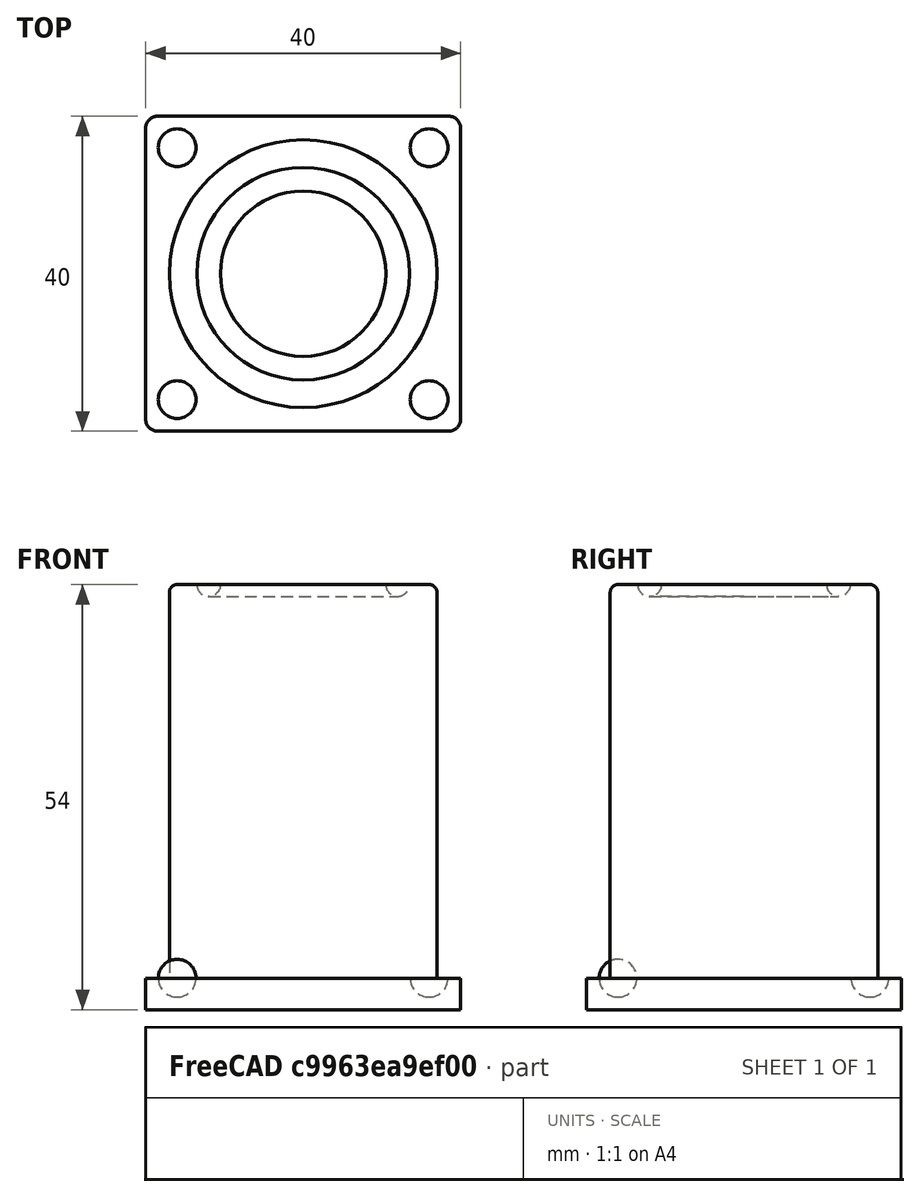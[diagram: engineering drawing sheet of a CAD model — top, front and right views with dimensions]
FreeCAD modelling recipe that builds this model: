
FCSTD DOCUMENT  (FreeCAD 0.21R33694 (Git))
Label: OJT1_T15R03
License: All rights reserved
LicenseURL: http://en.wikipedia.org/wiki/All_rights_reserved
objects: Part::Fillet×2, Part::Cut×2, Part::Box×1, Part::Cylinder×1, Part::Torus×1, Part::Sphere×1, Part::FeaturePython×1, Part::Fuse×1
note: 9 computed .brp shape members not serialized (recipe doc carries the construction recipe); baked Part::Feature solids carry a one-line shape summary decoded from their .brp

FEATURE [Part::Box] Box  label="Cube"
  AttacherType = Attacher::AttachEngine3D
  Height = 4
  Length = 40
  Width = 40
FEATURE [Part::Cylinder] Cylinder
  Angle = 360
  AttacherType = Attacher::AttachEngine3D
  FirstAngle = 0
  Height = 50
  Radius = 17
  SecondAngle = 0
FEATURE [Part::Torus] Torus  label="part_cilindre"
  Angle1 = -180
  Angle2 = 180
  Angle3 = 360
  AttacherType = Attacher::AttachEngine3D
  Placement = pos=(0,0,50) rot=(0,0,1;0rad)
  Radius1 = 12
  Radius2 = 1.5
FEATURE [Part::Fillet] Fillet  label="cilindre_sense_acabar"
  Base = -> Box
  Edges = 4 edges r=1.5: [Edge1,Edge3,Edge5,Edge7]
FEATURE [Part::Fillet] Fillet001  label="cilindre"
  Base = -> Cylinder
  Edges = 1 edges r=1: [Edge3]
FEATURE [Part::Sphere] Sphere
  Angle1 = -90
  Angle2 = 90
  Angle3 = 360
  AttacherType = Attacher::AttachEngine3D
  Placement = pos=(4,4,4) rot=(0,0,1;0rad)
  Radius = 2.4
FEATURE [Part::FeaturePython] Array  # Draft array (typed FeaturePython)
  AlwaysSyncPlacement = false
  Angle = 360
  ArrayType = 0
  Axis = (0,0,1)
  Base = -> Sphere
  Center = (0,0,0)
  Count = 4
  ExpandArray = false
  Fuse = false
  IntervalAxis = (0,0,0)
  IntervalX = (32,0,0)
  IntervalY = (0,32,0)
  IntervalZ = (0,0,100)
  NumberCircles = 3
  NumberPolar = 5
  NumberX = 2
  NumberY = 2
  NumberZ = 1
  PlacementList = 4 placements: [(4,4,4),(4,36,4),(36,4,4),(36,36,4)]
  RadialDistance = 50
  ScaleList = (4) [(1,1,1),(1,1,1),(1,1,1),(1,1,1)]
  Symmetry = 1
  TangentialDistance = 25
FEATURE [Part::Cut] Cut  label="base_acabada"
  Base = -> Fillet
  Refine = true
  Tool = -> Array
FEATURE [Part::Cut] Cut001  label="cilindre_acabat"
  Base = -> Fillet001
  Placement = pos=(20,20,4) rot=(0,0,1;0rad)
  Refine = true
  Tool = -> Torus
FEATURE [Part::Fuse] Fusion  label="objecte"
  Base = -> Cut
  Refine = true
  Tool = -> Cut001
